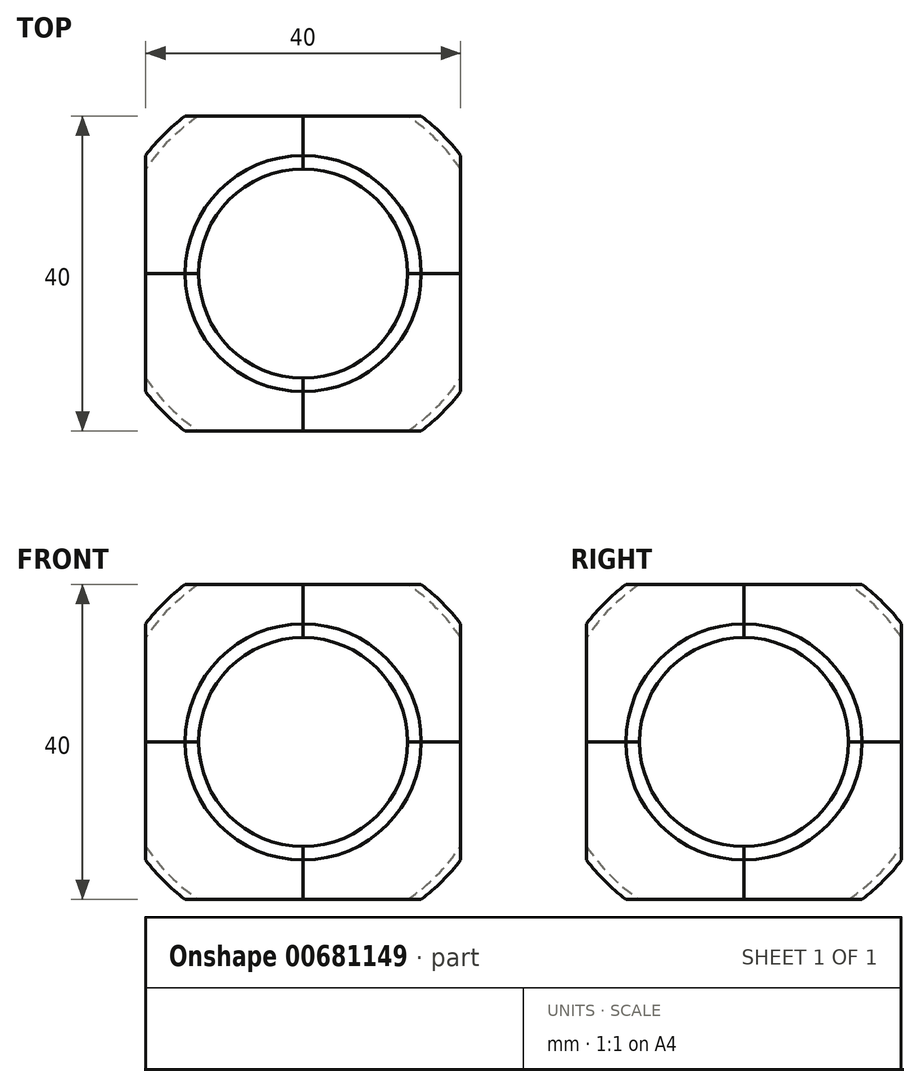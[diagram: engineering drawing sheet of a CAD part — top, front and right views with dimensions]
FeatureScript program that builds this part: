
annotation { "Feature Type Name" : "Feature", "Feature Type Description" : "" }
export const myFeature = defineFeature(function(context is Context, id is Id, definition is map)
    precondition{}
    {
        {
            var Q0;
            Q0=qCreatedBy(makeId("Front.planeOp"),FACE);
            var sketch = newSketch(context, id + "F0", { "sketchPlane" : qUnion([Q0])});
            skArc(sketch, "E0", {"start": v(0, -25) * mm, "mid": v(25, 0) * mm, "end": v(0, 25) * mm});
            skLineSegment(sketch, "E1", {"start": v(0, 25) * mm, "end": v(0, 24) * mm});
            skArc(sketch, "E2", {"start": v(0, -24) * mm, "mid": v(24, 0) * mm, "end": v(0, 24) * mm});
            skLineSegment(sketch, "E3.trimOffspring", {"start": v(0, -24) * mm, "end": v(0, -25) * mm});
            skSolve(sketch);
        }
        {
            var Q0;
            Q0=makeQuery(id+"F0.imprint","IMPRINT",FACE,{"disambiguationData":[TD([[makeQuery(id+"F0.imprint","IMPRINT",EDGE,{"derivedFrom":sQuery(id+"F0.wireOp",EDGE,"E0")}),1.0]])]});
            var Q1;
            Q1=sQuery(id+"F0.wireOp",EDGE,"E1");
            revolve(context, id + "F1", {"entities" : qUnion([Q0]), "axis" : qUnion([Q1]), "revolveType" : RevolveType.ONE_DIRECTION, "angle" : 90 * degree});
        }
        {
            var Q0;
            Q0=qCreatedBy(makeId("Front.planeOp"),FACE);
            var sketch = newSketch(context, id + "F2", { "sketchPlane" : qUnion([Q0])});
            skLineSegment(sketch, "E4.bottom", {"start": v(62.88, 46.28) * mm, "end": v(20, 46.28) * mm});
            skLineSegment(sketch, "E4.top", {"start": v(62.88, -47.42) * mm, "end": v(20, -47.42) * mm});
            skLineSegment(sketch, "E4.left", {"start": v(62.88, 46.28) * mm, "end": v(62.88, -47.42) * mm});
            skLineSegment(sketch, "E4.right", {"start": v(20, 46.28) * mm, "end": v(20, -47.42) * mm});
            skLineSegment(sketch, "E5.bottom", {"start": v(-22.72, 36.3) * mm, "end": v(29.87, 36.3) * mm});
            skLineSegment(sketch, "E5.top", {"start": v(-22.72, 20) * mm, "end": v(29.87, 20) * mm});
            skLineSegment(sketch, "E5.left", {"start": v(-22.72, 36.3) * mm, "end": v(-22.72, 20) * mm});
            skLineSegment(sketch, "E5.right", {"start": v(29.87, 36.3) * mm, "end": v(29.87, 20) * mm});
            skLineSegment(sketch, "E6.bottom", {"start": v(-45.88, 26.01) * mm, "end": v(0, 26.01) * mm});
            skLineSegment(sketch, "E6.top", {"start": v(-45.88, -39.73) * mm, "end": v(0, -39.73) * mm});
            skLineSegment(sketch, "E6.left", {"start": v(-45.88, 26.01) * mm, "end": v(-45.88, -39.73) * mm});
            skLineSegment(sketch, "E6.right", {"start": v(0, 26.01) * mm, "end": v(0, -39.73) * mm});
            skLineSegment(sketch, "E7.bottom", {"start": v(-26.15, -54.6) * mm, "end": v(41.02, -54.6) * mm});
            skLineSegment(sketch, "E7.top", {"start": v(-26.15, 0) * mm, "end": v(41.02, 0) * mm});
            skLineSegment(sketch, "E7.left", {"start": v(-26.15, -54.6) * mm, "end": v(-26.15, 0) * mm});
            skLineSegment(sketch, "E7.right", {"start": v(41.02, -54.6) * mm, "end": v(41.02, 0) * mm});
            skSolve(sketch);
        }
        {
            var Q0;
            Q0 = qSketchRegion(id + "F2", true);
            extrude(context, id + "F3", {"entities" : qUnion([Q0]), "operationType" : NewBodyOperationType.REMOVE, "endBound" : BoundingType.THROUGH_ALL, "oppositeDirection" : true, "depth" : 25 * mm, "offsetDistance" : 25 * mm, "hasSecondDirection" : true, "secondDirectionBound" : SecondDirectionBoundingType.THROUGH_ALL, "secondDirectionOppositeDirection" : false, "secondDirectionDepth" : 25 * mm});
        }
        {
            var Q0;
            Q0=qCreatedBy(makeId("Right.planeOp"),FACE);
            var sketch = newSketch(context, id + "F4", { "sketchPlane" : qUnion([Q0])});
            skLineSegment(sketch, "E8.bottom", {"start": v(-20, 20) * mm, "end": v(0, 20) * mm});
            skLineSegment(sketch, "E8.top", {"start": v(-20, 0) * mm, "end": v(0, 0) * mm});
            skLineSegment(sketch, "E8.left", {"start": v(-20, 20) * mm, "end": v(-20, 0) * mm});
            skLineSegment(sketch, "E8.right", {"start": v(0, 20) * mm, "end": v(0, 0) * mm});
            skSolve(sketch);
        }
        {
            var Q0;
            Q0 = qSketchRegion(id + "F4", true);
            extrude(context, id + "F5", {"entities" : qUnion([Q0]), "operationType" : NewBodyOperationType.INTERSECT, "endBound" : BoundingType.THROUGH_ALL, "depth" : 25 * mm, "offsetDistance" : 25 * mm});
        }
        {
            var Q0;
            Q0=makeQuery(id+"F1.opRevolve","SWEPT_BODY",BODY,{"disambiguationData":[OSD([sQuery(id+"F0.wireOp",EDGE,"E0"),sQuery(id+"F0.wireOp",EDGE,"E1"),sQuery(id+"F0.wireOp",EDGE,"E2"),sQuery(id+"F0.wireOp",EDGE,"E3.trimOffspring")])]});
            var Q1;
            Q1=qCreatedBy(makeId("Top.planeOp"),FACE);
            mirror(context, id + "F6", {"entities" : qUnion([Q0]), "mirrorPlane" : qUnion([Q1])});
        }
        {
            var Q0;
            Q0=makeQuery(id+"F1.opRevolve","SWEPT_BODY",BODY,{"disambiguationData":[OSD([sQuery(id+"F0.wireOp",EDGE,"E0"),sQuery(id+"F0.wireOp",EDGE,"E1"),sQuery(id+"F0.wireOp",EDGE,"E2"),sQuery(id+"F0.wireOp",EDGE,"E3.trimOffspring")])]});
            var Q1;
            Q1=makeQuery(id+"F6.opPattern","COPY",BODY,{"derivedFrom":makeQuery(id+"F1.opRevolve","SWEPT_BODY",BODY,{"disambiguationData":[OSD([sQuery(id+"F0.wireOp",EDGE,"E0"),sQuery(id+"F0.wireOp",EDGE,"E1"),sQuery(id+"F0.wireOp",EDGE,"E2"),sQuery(id+"F0.wireOp",EDGE,"E3.trimOffspring")])]}),"instanceName":"1"});
            var Q2;
            Q2=sQuery(id+"F0.wireOp",EDGE,"E1");
            circularPattern(context, id + "F7", {"entities" : qUnion([Q0, Q1]), "axis" : qUnion([Q2]), "angle" : 360 * degree, "instanceCount" : 4, "equalSpace" : true});
        }
    });
